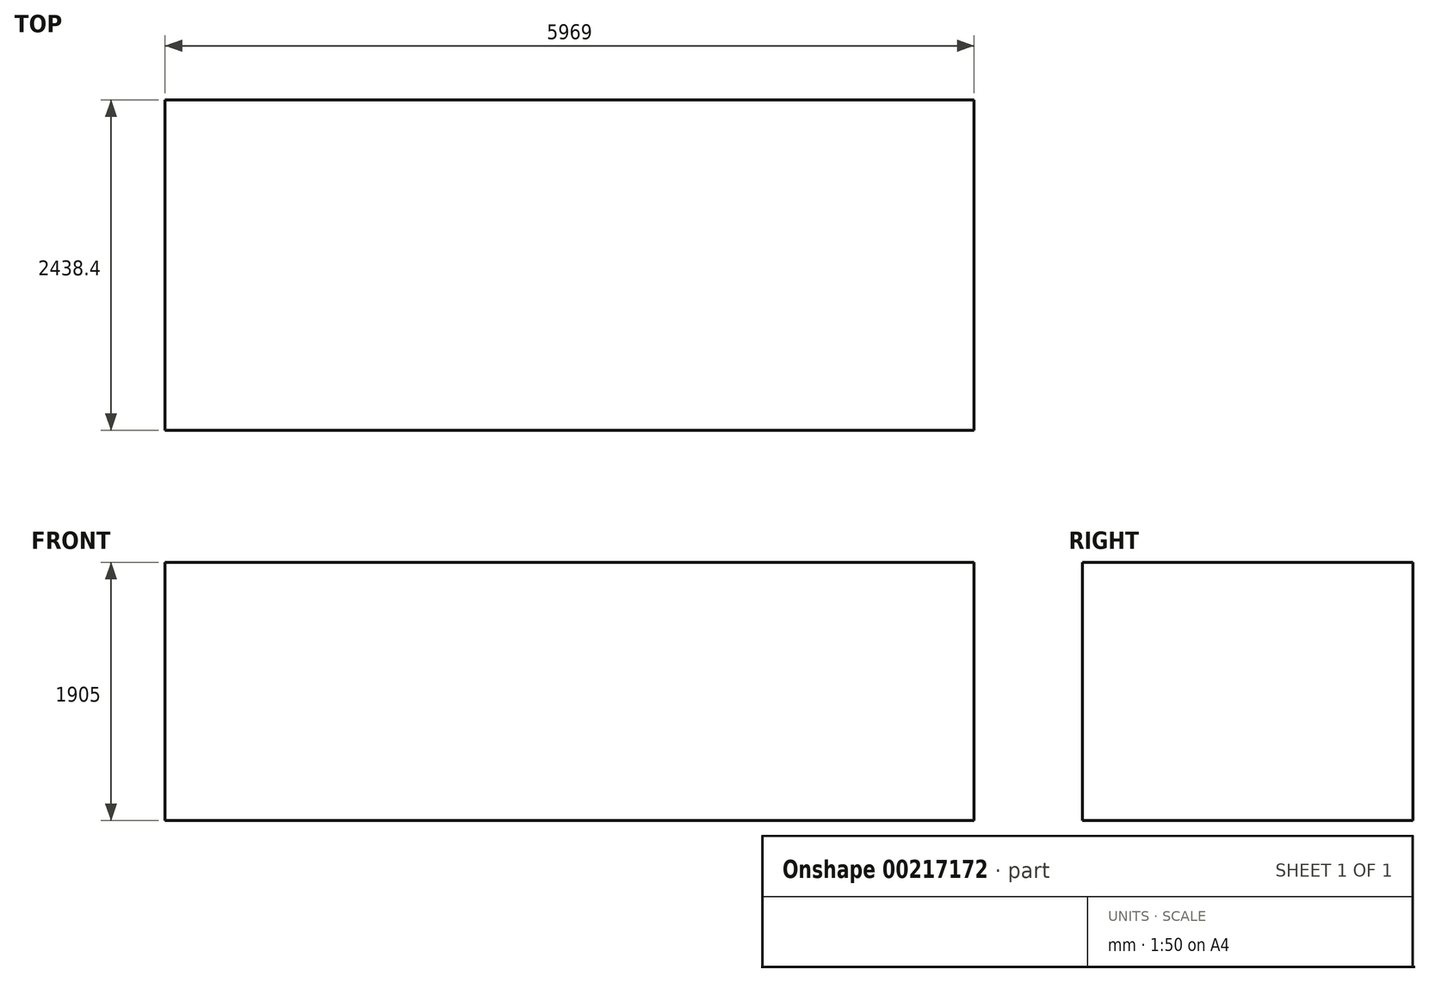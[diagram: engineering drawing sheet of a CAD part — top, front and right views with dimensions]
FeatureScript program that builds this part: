
annotation { "Feature Type Name" : "Feature", "Feature Type Description" : "" }
export const myFeature = defineFeature(function(context is Context, id is Id, definition is map)
    precondition{}
    {
        {
            var Q0;
            Q0=qCreatedBy(makeId("Front.planeOp"),FACE);
            var sketch = newSketch(context, id + "F0", { "sketchPlane" : qUnion([Q0])});
            skLineSegment(sketch, "E0.bottom", {"start": v(0, 0) * mm, "end": v(5969, 0) * mm});
            skLineSegment(sketch, "E0.top", {"start": v(0, 1905) * mm, "end": v(5969, 1905) * mm});
            skLineSegment(sketch, "E0.left", {"start": v(0, 0) * mm, "end": v(0, 1905) * mm});
            skLineSegment(sketch, "E0.right", {"start": v(5969, 0) * mm, "end": v(5969, 1905) * mm});
            skSolve(sketch);
        }
        {
            var Q0;
            Q0 = qSketchRegion(id + "F0", true);
            extrude(context, id + "F1", {"entities" : qUnion([Q0]), "depth" : 2438.4 * mm});
        }
    });
